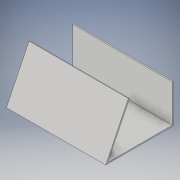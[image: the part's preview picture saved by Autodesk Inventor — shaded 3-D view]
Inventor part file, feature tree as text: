
AUTODESK INVENTOR PART (.ipt)
format: ipt  version: 2018 (Build 220112000, 112)  size: 101,376 bytes
history: native  units: in
note: dims shown in document units (in); Inventor stores cm internally (conversion verified against a paired STEP export)
features: extrude x1, sketch x1
ambient origin geometry x8: Origin, YZ Plane, XZ Plane, XY Plane, X Axis, Y Axis, Z Axis, Center Point
bodies: Solid1 (feature_tree)
feature tree (2):
  extrude  "Extrusion1"  Depth=0.1in
  sketch  "Sketch1"  dims[d0=5.0in d1=0.1in d2=0.1in d3=4.0in d4=0.4398in d5=3.0in d6=0.1in d7=7.7in d8=0.0in]
